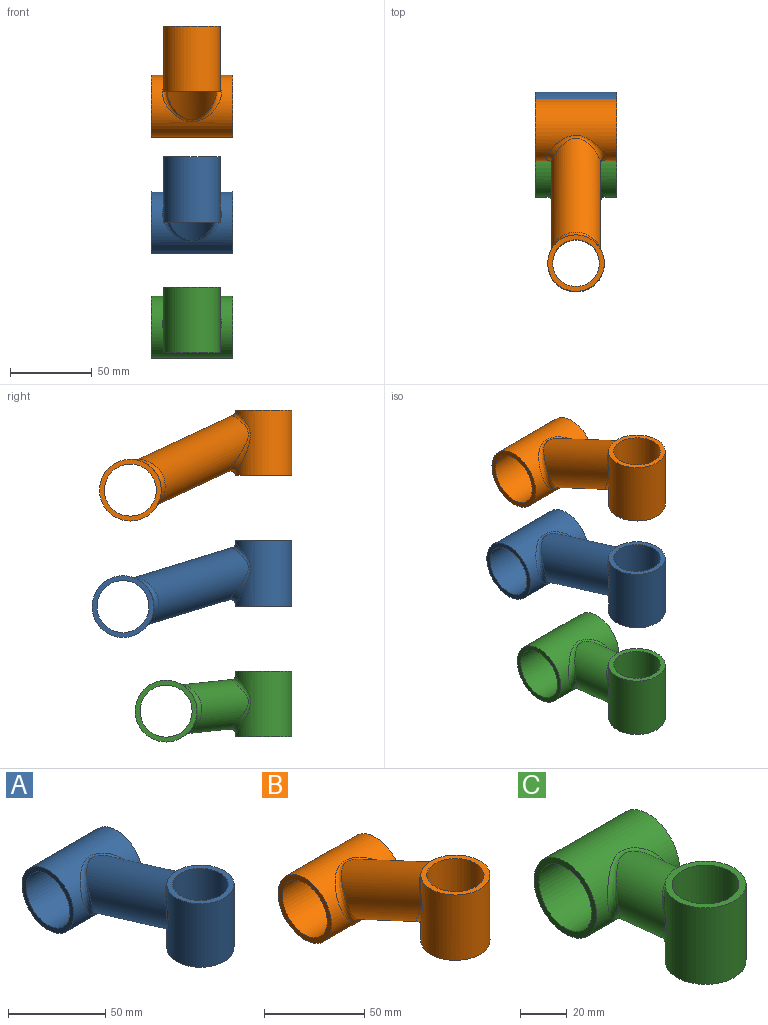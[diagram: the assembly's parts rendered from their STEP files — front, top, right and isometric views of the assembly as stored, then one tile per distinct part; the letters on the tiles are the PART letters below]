
ASSEMBLY  parts=3 mates=4
PART A: 14 faces, bbox 50x122.3x59.2 mm
  f0: cylinder r=17.3mm len=40mm, axis (0,0,1), area 3302.3mm2, adj f1,f3,f10
  f1: plane 34.6x34.6mm, normal (0,0,-1), area 297.8mm2, adj f0,f2
  f2: cylinder r=14.3mm len=40mm, axis (0,0,1), area 3594mm2, adj f1,f3
  f3: plane 34.6x34.6mm, normal (0,0,1), area 297.8mm2, adj f0,f2
  f4: cylinder r=18.9mm len=50mm, axis (-1,0,0), area 4954.5mm2, adj f6,f7,f9
  f5: cylinder r=15.9mm len=50mm, axis (-1,0,0), area 4995.1mm2, adj f6,f7
  f6: plane 37.8x37.8mm, normal (1,0,0), area 328mm2, adj f4,f5
  f7: plane 37.8x37.8mm, normal (-1,0,0), area 328mm2, adj f4,f5
  f8: cylinder r=15mm len=73.94mm, axis (0,-0.96,0.29), area 5319mm2, adj f9,f10
  f9: bspline ~36.03x29.73mm, area 347.5mm2, adj f4,f8
  f10: bspline ~37.65x30.69mm, area 345.5mm2, adj f0,f8
  f11: cylinder r=17.3mm len=25.1mm, axis (0,0,1), area 508.3mm2, adj f13
  f12: cylinder r=18.9mm len=24mm, axis (-1,0,0), area 479.8mm2, adj f13
  f13: cylinder r=12mm len=67.21mm, axis (0,-0.96,0.29), area 4336.6mm2, adj f11,f12
PART B: 15 faces, bbox 50x117.8x67.9 mm
  f0: cylinder r=17.3mm len=40mm, axis (0,0,1), area 3246.1mm2, adj f1,f3,f10
  f1: plane 34.61x34.61mm, normal (0,0,-1), area 297.8mm2, adj f0,f2,f11
  f2: cylinder r=14.3mm len=40mm, axis (0,0,1), area 3594mm2, adj f1,f3
  f3: plane 34.6x34.6mm, normal (0,0,1), area 297.8mm2, adj f0,f2
  f4: cylinder r=18.9mm len=50mm, axis (-1,0,0), area 4954.5mm2, adj f6,f7,f9
  f5: cylinder r=15.9mm len=50mm, axis (-1,0,0), area 4995.1mm2, adj f6,f7
  f6: plane 37.8x37.8mm, normal (1,0,0), area 328mm2, adj f4,f5
  f7: plane 37.8x37.8mm, normal (-1,0,0), area 328mm2, adj f4,f5
  f8: cylinder r=15mm len=74.44mm, axis (0,-0.91,0.42), area 5235.1mm2, adj f9,f10,f11
  f9: bspline ~36.03x28.41mm, area 347.5mm2, adj f4,f8
  f10: bspline ~39.37x30.68mm, area 331.8mm2, adj f0,f8,f11
  f11: bspline ~5.79x4.52mm, area 24.5mm2, adj f1,f8,f10
  f12: cylinder r=17.3mm len=26.48mm, axis (0,0,1), area 536.9mm2, adj f14
  f13: cylinder r=18.9mm len=24mm, axis (-1,0,0), area 479.8mm2, adj f14
  f14: cylinder r=12mm len=67.18mm, axis (0,-0.91,0.42), area 4271.9mm2, adj f12,f13
PART C: 14 faces, bbox 50x95.9x43.2 mm
  f0: cylinder r=17.3mm len=40mm, axis (0,0,1), area 3341.3mm2, adj f1,f3,f10
  f1: plane 34.6x34.6mm, normal (0,0,-1), area 297.8mm2, adj f0,f2
  f2: cylinder r=14.3mm len=40mm, axis (0,0,1), area 3594mm2, adj f1,f3
  f3: plane 34.6x34.6mm, normal (0,0,1), area 297.8mm2, adj f0,f2
  f4: cylinder r=18.9mm len=50mm, axis (-1,0,0), area 4954.5mm2, adj f6,f7,f9
  f5: cylinder r=15.9mm len=50mm, axis (-1,0,0), area 4995.1mm2, adj f6,f7
  f6: plane 37.8x37.8mm, normal (1,0,0), area 328mm2, adj f4,f5
  f7: plane 37.8x37.8mm, normal (-1,0,0), area 328mm2, adj f4,f5
  f8: cylinder r=15mm len=41.07mm, axis (0,-0.99,0.1), area 2550.1mm2, adj f9,f10
  f9: bspline ~36.03x30.92mm, area 347.5mm2, adj f4,f8
  f10: bspline ~36.22x30.69mm, area 337.7mm2, adj f0,f8
  f11: cylinder r=17.3mm len=24.13mm, axis (0,0,1), area 488.8mm2, adj f13
  f12: cylinder r=18.9mm len=24mm, axis (-1,0,0), area 479.8mm2, adj f13
  f13: cylinder r=12mm len=35.27mm, axis (0,-0.99,0.1), area 2120.3mm2, adj f11,f12
PLACE A t=(25.5,-53.95,60.56)mm fixed
PLACE B rot(axis=(0,0,1),0deg) t=(25.5,-53.95,143.56)mm
PLACE C t=(25.5,-53.95,-23.44)mm
MATE slider C.f0 <-> A.f0  axis (0,0,1) through (25.5,-53.95,-25.44)mm
MATE cylindrical B.f0 <-> A.f2  axis (0,0,1) through (25.5,-53.95,154.56)mm
MATE planar B.f1 <-> A.f0  axis (0,0,-1) through (27.86,-36.81,114.56)mm
MATE planar C.f0 <-> A.f2  axis (0,0,1) through (25.5,-53.95,-5.44)mm
